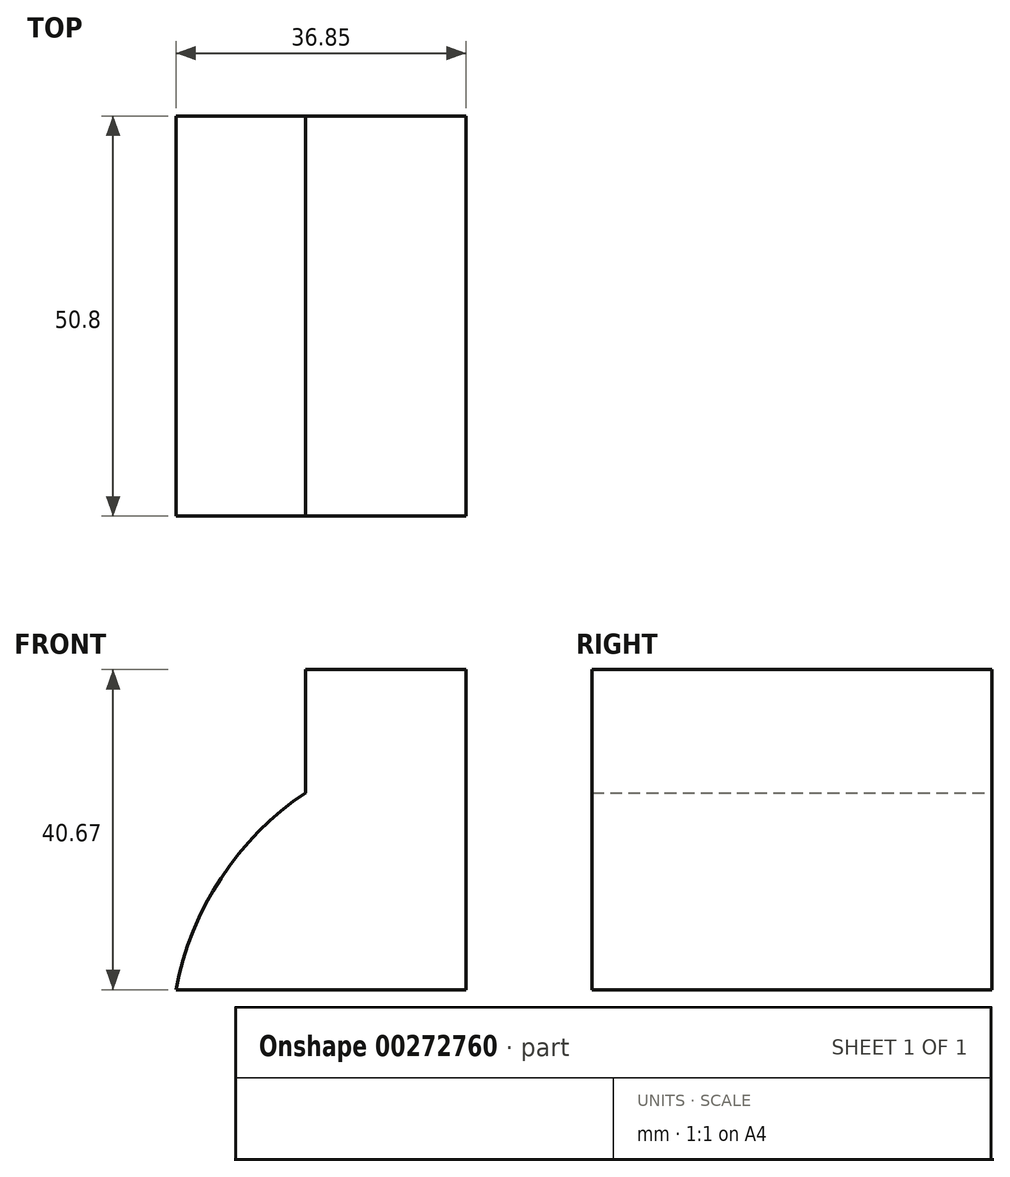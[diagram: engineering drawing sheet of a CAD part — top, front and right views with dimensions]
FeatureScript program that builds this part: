
annotation { "Feature Type Name" : "Feature", "Feature Type Description" : "" }
export const myFeature = defineFeature(function(context is Context, id is Id, definition is map)
    precondition{}
    {
        {
            var Q0;
            Q0=qCreatedBy(makeId("Front.planeOp"),FACE);
            var sketch = newSketch(context, id + "F0", { "sketchPlane" : qUnion([Q0])});
            skLineSegment(sketch, "E0", {"start": v(0, 40.67) * mm, "end": v(0, -1.9) * mm});
            skLineSegment(sketch, "E1", {"start": v(0, 0) * mm, "end": v(-38.2, 0) * mm});
            skLineSegment(sketch, "E2", {"start": v(0, 40.67) * mm, "end": v(-20.43, 40.67) * mm});
            skLineSegment(sketch, "E3", {"start": v(-20.43, 40.67) * mm, "end": v(-20.43, 25.02) * mm});
            skArc(sketch, "E4", {"start": v(-20.43, 25.02) * mm, "mid": v(-31.15, 14.15) * mm, "end": v(-36.85, 0) * mm});
            skSolve(sketch);
        }
        {
            var Q0;
            {var subQ0=sQuery(id+"F0.wireOp",EDGE,"E2");Q0=makeQuery(id+"F0.imprint","IMPRINT",FACE,{"disambiguationData":[TD([[makeQuery(id+"F0.imprint","IMPRINT",EDGE,{"derivedFrom":subQ0}),1.0]])]});}
            extrude(context, id + "F1", {"entities" : qUnion([Q0]), "depth" : 50.8 * mm});
        }
    });
